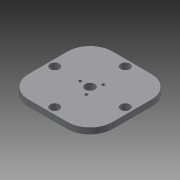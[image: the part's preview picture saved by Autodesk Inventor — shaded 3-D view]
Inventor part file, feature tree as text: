
AUTODESK INVENTOR PART (.ipt)
format: ipt  version: 2015 (Build 190159000, 159)  size: 117,248 bytes
history: native  units: in
note: dims shown in document units (in); Inventor stores cm internally (conversion verified against a paired STEP export)
features: extrude x1, fillet x1, sketch x1
ambient origin geometry x8: Origin, YZ Plane, XZ Plane, XY Plane, X Axis, Y Axis, Z Axis, Center Point
bodies: Body1 (feature_tree)
feature tree (3):
  extrude  "Extrusion6"  TaperAngle=120.0deg  [1 undecoded]
  fillet  "Fillet1"  Radius=0.4375in
  sketch  "Sketch3"  dims[d19=120.0deg d20=120.0deg d21=0.4375in d22=0.4375in d23=0.4375in d24=0.1174in d25=0.1174in d26=0.1174in d27=3.1496in d28=3.1496in d29=0.3937in d30=0.3937in d31=3.75in d32=3.75in d33=0.25in d34=0.0in d35=1.0in d36=0.4134in]
note: 1 required parameter value undecoded (feature->parameter linkage not recoverable at this tier; creation-order binding heuristic only, values carry confidence <= 0.55)
